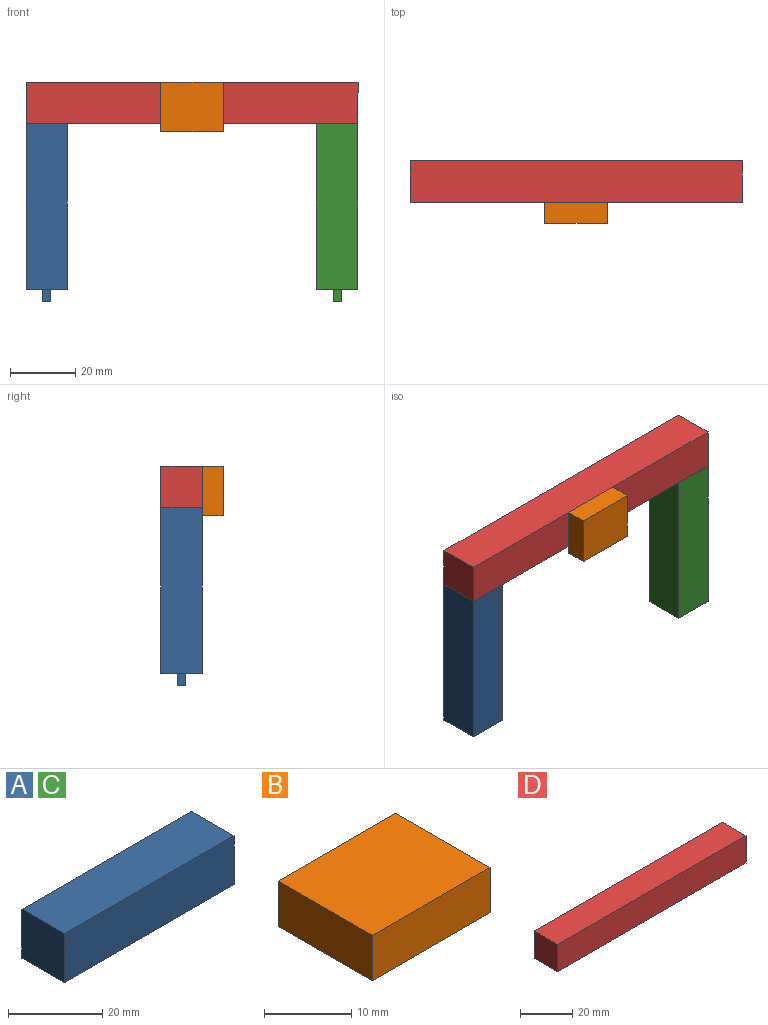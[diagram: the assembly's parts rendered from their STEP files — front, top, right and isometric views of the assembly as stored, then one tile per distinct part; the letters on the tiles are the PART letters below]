
ASSEMBLY  parts=4 mates=3
PART A: 11 faces, bbox 54.6x12.7x12.7 mm
  f0: plane 50.8x12.7mm, normal (0,1,0), area 645.2mm2, adj f1,f3,f4,f5
  f1: plane 12.7x12.7mm, normal (-1,0,0), area 161.3mm2, adj f0,f2,f4,f5
  f2: plane 50.8x12.7mm, normal (0,-1,0), area 645.2mm2, adj f1,f3,f4,f5
  f3: plane 12.7x12.7mm, normal (1,0,0), area 154.8mm2, adj f0,f2,f4,f5,f6,f7,f8,f9
  f4: plane 50.8x12.7mm, normal (0,0,1), area 645.2mm2, adj f0,f1,f2,f3
  f5: plane 50.8x12.7mm, normal (0,0,-1), area 645.2mm2, adj f0,f1,f2,f3
  f6: plane 3.81x2.54mm, normal (0,1,0), area 9.7mm2, adj f3,f7,f9,f10
  f7: plane 3.81x2.54mm, normal (0,0,1), area 9.7mm2, adj f3,f6,f8,f10
  f8: plane 3.81x2.54mm, normal (0,-1,0), area 9.7mm2, adj f3,f7,f9,f10
  f9: plane 3.81x2.54mm, normal (0,0,-1), area 9.7mm2, adj f3,f6,f8,f10
  f10: plane 2.54x2.54mm, normal (1,0,0), area 6.5mm2, adj f6,f7,f8,f9
PART B: 6 faces, bbox 19.1x15.2x6.4 mm
  f0: plane 15.24x6.35mm, normal (-1,0,0), area 96.8mm2, adj f1,f3,f4,f5
  f1: plane 19.05x6.35mm, normal (0,-1,0), area 121mm2, adj f0,f2,f4,f5
  f2: plane 15.24x6.35mm, normal (1,0,0), area 96.8mm2, adj f1,f3,f4,f5
  f3: plane 19.05x6.35mm, normal (0,1,0), area 121mm2, adj f0,f2,f4,f5
  f4: plane 19.05x15.24mm, normal (0,0,1), area 290.3mm2, adj f0,f1,f2,f3
  f5: plane 19.05x15.24mm, normal (0,0,-1), area 290.3mm2, adj f0,f1,f2,f3
PART C: same geometry as A
PART D: 6 faces, bbox 101.6x12.7x12.7 mm
  f0: plane 101.6x12.7mm, normal (0,1,0), area 1290.3mm2, adj f1,f3,f4,f5
  f1: plane 12.7x12.7mm, normal (-1,0,0), area 161.3mm2, adj f0,f2,f4,f5
  f2: plane 101.6x12.7mm, normal (0,-1,0), area 1290.3mm2, adj f1,f3,f4,f5
  f3: plane 12.7x12.7mm, normal (1,0,0), area 161.3mm2, adj f0,f2,f4,f5
  f4: plane 101.6x12.7mm, normal (0,0,1), area 1290.3mm2, adj f0,f1,f2,f3
  f5: plane 101.6x12.7mm, normal (0,0,-1), area 1290.3mm2, adj f0,f1,f2,f3
PLACE A rot(axis=(0.58,0.58,-0.58),120deg) t=(8.43,-11.63,-39.26)mm
PLACE B rot(axis=(-1,0,0),90deg) t=(25.01,-30.68,-16.9)mm
PLACE C rot(axis=(0.58,0.58,-0.58),120deg) t=(97.33,-11.63,-39.26)mm
PLACE D rot(axis=(1,0,0),90deg) t=(9.37,-11.63,-66.72)mm
MATE fastened D.f4 <-> B.f4  axis (0,-1,0) through (50.13,-24.33,-9.43)mm
MATE fastened D.f2 <-> A.f1  axis (0,0,-1) through (-0.67,-11.63,-22.13)mm
MATE fastened D.f2 <-> C.f1  axis (0,0,-1) through (100.93,-11.63,-22.13)mm
